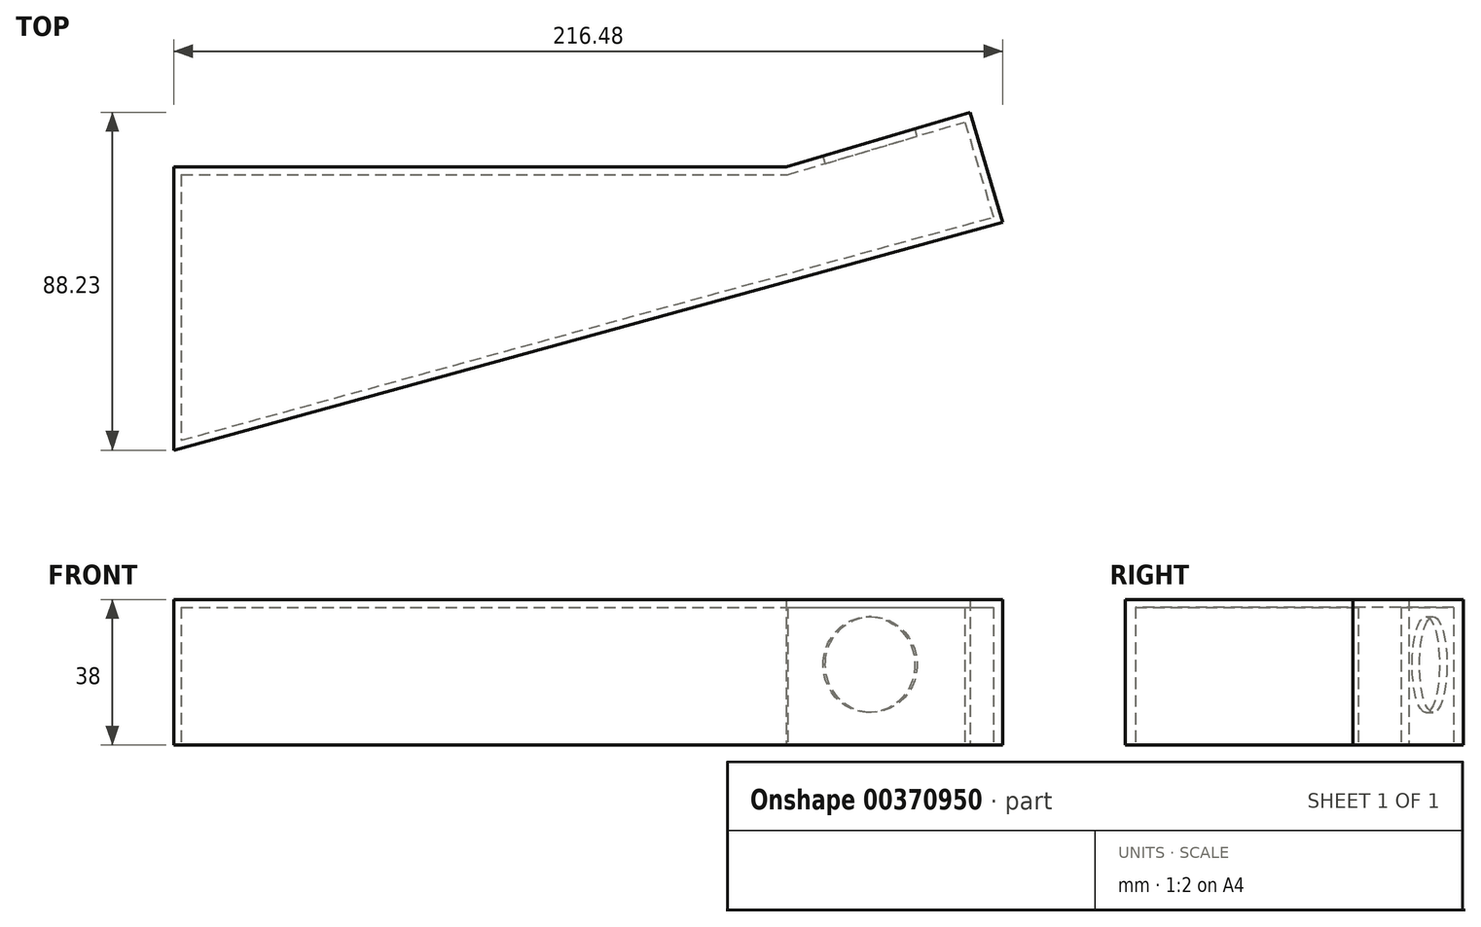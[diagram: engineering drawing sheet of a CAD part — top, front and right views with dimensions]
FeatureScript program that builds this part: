
annotation { "Feature Type Name" : "Feature", "Feature Type Description" : "" }
export const myFeature = defineFeature(function(context is Context, id is Id, definition is map)
    precondition{}
    {
        {
            var Q0;
            Q0=qCreatedBy(makeId("Top.planeOp"),FACE);
            var sketch = newSketch(context, id + "F0", { "sketchPlane" : qUnion([Q0])});
            skLineSegment(sketch, "E0.bottom", {"start": v(0, 0) * mm, "end": v(160, 0) * mm});
            skLineSegment(sketch, "E0.top", {"start": v(0, -73.96) * mm, "end": v(160, -30) * mm});
            skLineSegment(sketch, "E0.left", {"start": v(0, 0) * mm, "end": v(0, -73.96) * mm});
            skLineSegment(sketch, "E1", {"start": v(160, 0) * mm, "end": v(207.92, 14.27) * mm});
            skLineSegment(sketch, "E2", {"start": v(207.92, 14.27) * mm, "end": v(216.48, -14.48) * mm});
            skLineSegment(sketch, "E3", {"start": v(216.48, -14.48) * mm, "end": v(160, -30) * mm});
            skSolve(sketch);
        }
        {
            var Q0;
            Q0 = qSketchRegion(id + "F0", true);
            extrude(context, id + "F1", {"entities" : qUnion([Q0]), "depth" : 38 * mm});
        }
        {
            var Q0;
            Q0=makeQuery(id+"F1.opExtrude","CAP_FACE",FACE,{"disambiguationData":[OSD([sQuery(id+"F0.wireOp",EDGE,"E0.bottom"),sQuery(id+"F0.wireOp",EDGE,"E0.top"),sQuery(id+"F0.wireOp",EDGE,"E0.left"),sQuery(id+"F0.wireOp",EDGE,"E1"),sQuery(id+"F0.wireOp",EDGE,"E2"),sQuery(id+"F0.wireOp",EDGE,"E3")])],"isStart":true});
            shell(context, id + "F2", {"entities" : qUnion([Q0]), "thickness" : 2 * mm});
        }
        {
            var Q0;
            Q0=makeQuery(id+"F1.opExtrude","SWEPT_FACE",FACE,{"disambiguationData":[OSD([sQuery(id+"F0.wireOp",EDGE,"E1")])]});
            var sketch = newSketch(context, id + "F3", { "sketchPlane" : qUnion([Q0])});
            skCircle(sketch, "E4", {"center": v(-175.84, 21) * mm, "radius": 12.5 * mm});
            skSolve(sketch);
        }
        {
            var Q0;
            Q0 = qSketchRegion(id + "F3", true);
            extrude(context, id + "F4", {"entities" : qUnion([Q0]), "operationType" : NewBodyOperationType.REMOVE, "oppositeDirection" : true, "depth" : 25 * mm});
        }
    });
